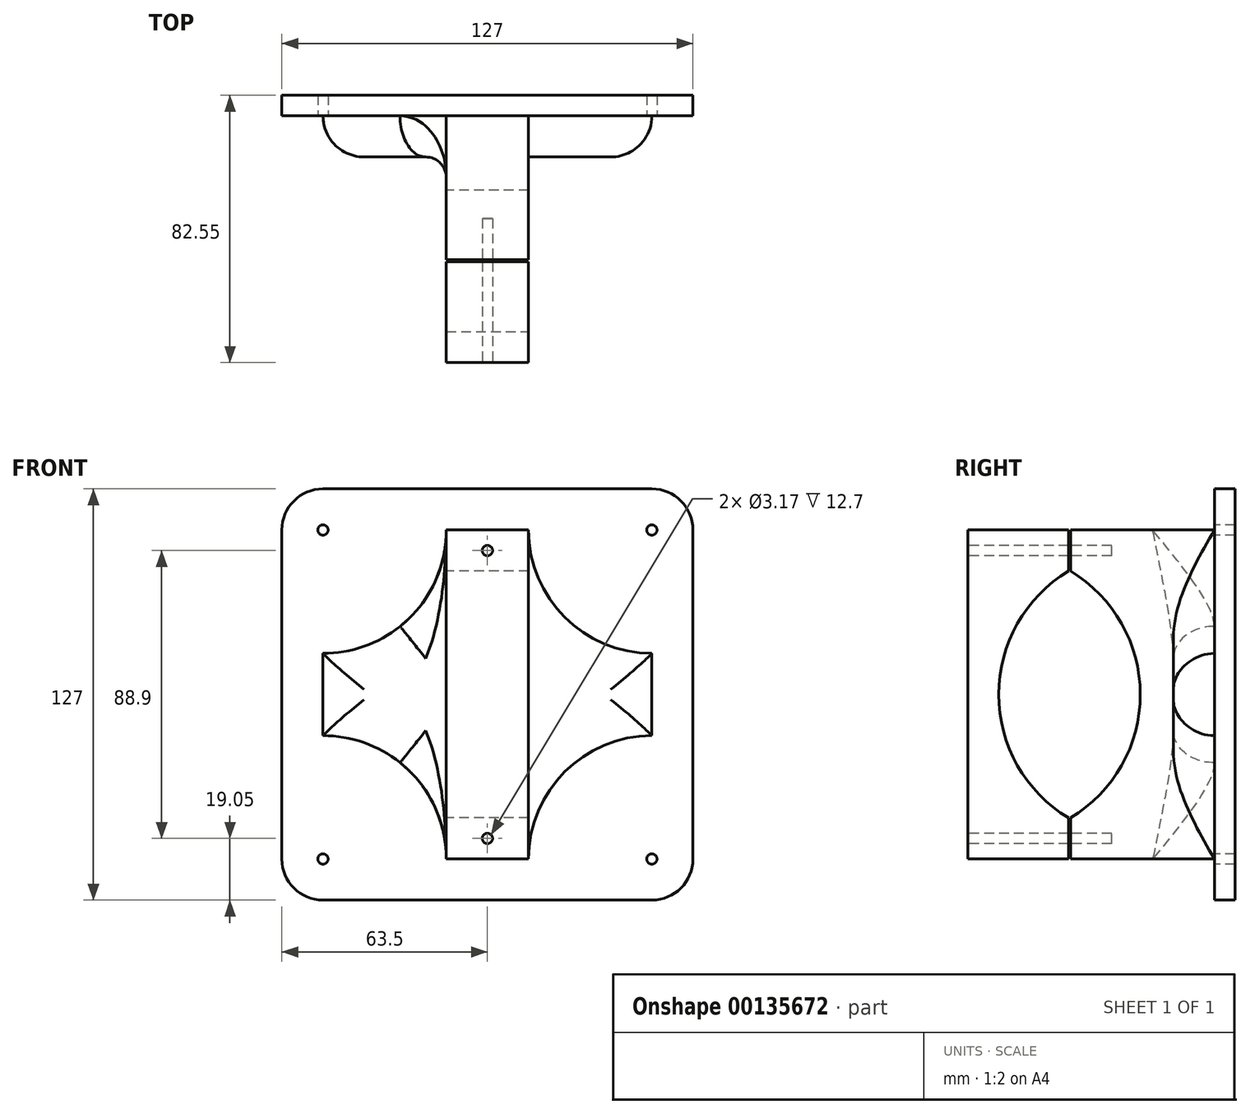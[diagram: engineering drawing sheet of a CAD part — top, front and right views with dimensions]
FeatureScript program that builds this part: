
annotation { "Feature Type Name" : "Feature", "Feature Type Description" : "" }
export const myFeature = defineFeature(function(context is Context, id is Id, definition is map)
    precondition{}
    {
        {
            var Q0;
            Q0=qCreatedBy(makeId("Front.planeOp"),FACE);
            var sketch = newSketch(context, id + "F0", { "sketchPlane" : qUnion([Q0])});
            skLineSegment(sketch, "E0.bottom", {"start": v(63.5, 63.5) * mm, "end": v(-63.5, 63.5) * mm});
            skLineSegment(sketch, "E0.top", {"start": v(63.5, -63.5) * mm, "end": v(-63.5, -63.5) * mm});
            skLineSegment(sketch, "E0.left", {"start": v(63.5, 63.5) * mm, "end": v(63.5, -63.5) * mm});
            skLineSegment(sketch, "E0.right", {"start": v(-63.5, 63.5) * mm, "end": v(-63.5, -63.5) * mm});
            skPoint(sketch, "E0.middle", {"position": v(0, 0) * mm});
            skSolve(sketch);
        }
        {
            var Q0;
            Q0 = qSketchRegion(id + "F0", true);
            extrude(context, id + "F1", {"entities" : qUnion([Q0]), "depth" : 6.35 * mm});
        }
        {
            var Q0;
            Q0=makeQuery(id+"F1.opExtrude","SWEPT_EDGE",EDGE,{"disambiguationData":[OSD([sQuery(id+"F0.wireOp",EDGE,"E0.bottom"),sQuery(id+"F0.wireOp",EDGE,"E0.right")])]});
            var Q1;
            Q1=makeQuery(id+"F1.opExtrude","SWEPT_EDGE",EDGE,{"disambiguationData":[OSD([sQuery(id+"F0.wireOp",EDGE,"E0.bottom"),sQuery(id+"F0.wireOp",EDGE,"E0.left")])]});
            var Q2;
            Q2=makeQuery(id+"F1.opExtrude","SWEPT_EDGE",EDGE,{"disambiguationData":[OSD([sQuery(id+"F0.wireOp",EDGE,"E0.top"),sQuery(id+"F0.wireOp",EDGE,"E0.left")])]});
            var Q3;
            Q3=makeQuery(id+"F1.opExtrude","SWEPT_EDGE",EDGE,{"disambiguationData":[OSD([sQuery(id+"F0.wireOp",EDGE,"E0.top"),sQuery(id+"F0.wireOp",EDGE,"E0.right")])]});
            fillet(context, id + "F2", {"entities" : qUnion([Q0, Q1, Q2, Q3]), "radius" : 12.7 * mm, "tangentPropagation" : true, "allowEdgeOverflow" : false});
        }
        {
            var Q0;
            Q0=makeQuery(id+"F1.opExtrude","CAP_FACE",FACE,{"disambiguationData":[OSD([sQuery(id+"F0.wireOp",EDGE,"E0.bottom"),sQuery(id+"F0.wireOp",EDGE,"E0.top"),sQuery(id+"F0.wireOp",EDGE,"E0.left"),sQuery(id+"F0.wireOp",EDGE,"E0.right")])],"isStart":false});
            var sketch = newSketch(context, id + "F3", { "sketchPlane" : qUnion([Q0])});
            skPoint(sketch, "E1", {"position": v(-50.8, 50.8) * mm});
            skPoint(sketch, "E2", {"position": v(50.8, 50.8) * mm});
            skPoint(sketch, "E3", {"position": v(50.8, -50.8) * mm});
            skPoint(sketch, "E4", {"position": v(-50.8, -50.8) * mm});
            skSolve(sketch);
        }
        {
            var Q0;
            Q0=sQuery(id+"F3.wireOp",VERTEX,"E2");
            var Q1;
            Q1=sQuery(id+"F3.wireOp",VERTEX,"E3");
            var Q2;
            Q2=sQuery(id+"F3.wireOp",VERTEX,"E4");
            var Q3;
            Q3=sQuery(id+"F3.wireOp",VERTEX,"E1");
            var Q4;
            Q4=makeQuery(id+"F1.opExtrude","SWEPT_BODY",BODY,{"disambiguationData":[OSD([sQuery(id+"F0.wireOp",EDGE,"E0.bottom"),sQuery(id+"F0.wireOp",EDGE,"E0.top"),sQuery(id+"F0.wireOp",EDGE,"E0.left"),sQuery(id+"F0.wireOp",EDGE,"E0.right")])]});
            hole(context, id + "F4", {"style" : HoleStyle.SIMPLE, "endStyle" : HoleEndStyle.THROUGH, "holeDiameter" : 3.17 * mm, "locations" : qUnion([Q0, Q1, Q2, Q3]), "scope" : qUnion([Q4]), "isTappedThrough" : true});
        }
        {
            var Q0;
            Q0=makeQuery(id+"F1.opExtrude","CAP_FACE",FACE,{"disambiguationData":[OSD([sQuery(id+"F0.wireOp",EDGE,"E0.bottom"),sQuery(id+"F0.wireOp",EDGE,"E0.top"),sQuery(id+"F0.wireOp",EDGE,"E0.left"),sQuery(id+"F0.wireOp",EDGE,"E0.right")])],"isStart":false});
            var sketch = newSketch(context, id + "F5", { "sketchPlane" : qUnion([Q0])});
            skLineSegment(sketch, "E5.bottom", {"start": v(50.8, 12.7) * mm, "end": v(-50.8, 12.7) * mm});
            skLineSegment(sketch, "E5.top", {"start": v(50.8, -12.7) * mm, "end": v(-50.8, -12.7) * mm});
            skLineSegment(sketch, "E5.left", {"start": v(50.8, 12.7) * mm, "end": v(50.8, -12.7) * mm});
            skLineSegment(sketch, "E5.right", {"start": v(-50.8, 12.7) * mm, "end": v(-50.8, -12.7) * mm});
            skPoint(sketch, "E5.middle", {"position": v(0, 0) * mm});
            skLineSegment(sketch, "E6.bottom", {"start": v(-12.7, 50.8) * mm, "end": v(12.7, 50.8) * mm});
            skLineSegment(sketch, "E6.top", {"start": v(-12.7, -50.8) * mm, "end": v(12.7, -50.8) * mm});
            skLineSegment(sketch, "E6.left", {"start": v(-12.7, 50.8) * mm, "end": v(-12.7, -50.8) * mm});
            skLineSegment(sketch, "E6.right", {"start": v(12.7, 50.8) * mm, "end": v(12.7, -50.8) * mm});
            skArc(sketch, "E7", {"start": v(-50.8, 12.7) * mm, "mid": v(-23.86, 23.86) * mm, "end": v(-12.7, 50.8) * mm});
            skArc(sketch, "E8", {"start": v(12.7, 50.8) * mm, "mid": v(23.86, 23.86) * mm, "end": v(50.8, 12.7) * mm});
            skArc(sketch, "E9", {"start": v(50.8, -12.7) * mm, "mid": v(23.86, -23.86) * mm, "end": v(12.7, -50.8) * mm});
            skArc(sketch, "E10", {"start": v(-12.7, -50.8) * mm, "mid": v(-23.86, -23.86) * mm, "end": v(-50.8, -12.7) * mm});
            skSolve(sketch);
        }
        {
            var Q0;
            {var subQ0=sQuery(id+"F5.wireOp",EDGE,"E8");Q0=makeQuery(id+"F5.imprint","IMPRINT",FACE,{"disambiguationData":[TD([[makeQuery(id+"F5.imprint","IMPRINT",EDGE,{"derivedFrom":subQ0}),-1.0]])]});}
            var Q1;
            {var subQ0=sQuery(id+"F5.wireOp",EDGE,"E7");Q1=makeQuery(id+"F5.imprint","IMPRINT",FACE,{"disambiguationData":[TD([[makeQuery(id+"F5.imprint","IMPRINT",EDGE,{"derivedFrom":subQ0}),-1.0]])]});}
            var Q2;
            {var subQ0=sQuery(id+"F5.wireOp",EDGE,"E9");Q2=makeQuery(id+"F5.imprint","IMPRINT",FACE,{"disambiguationData":[TD([[makeQuery(id+"F5.imprint","IMPRINT",EDGE,{"derivedFrom":subQ0}),-1.0]])]});}
            var Q3;
            {var subQ0=sQuery(id+"F5.wireOp",EDGE,"E10");Q3=makeQuery(id+"F5.imprint","IMPRINT",FACE,{"disambiguationData":[TD([[makeQuery(id+"F5.imprint","IMPRINT",EDGE,{"derivedFrom":subQ0}),-1.0]])]});}
            var Q4;
            {var subQ0=sQuery(id+"F5.wireOp",EDGE,"E5.left");Q4=makeQuery(id+"F5.imprint","IMPRINT",FACE,{"disambiguationData":[TD([[makeQuery(id+"F5.imprint","IMPRINT",EDGE,{"derivedFrom":subQ0}),-1.0]])]});}
            var Q5;
            {var subQ5=sQuery(id+"F5.wireOp",EDGE,"E6.bottom");Q5=makeQuery(id+"F5.imprint","IMPRINT",FACE,{"disambiguationData":[TD([[makeQuery(id+"F5.imprint","IMPRINT",EDGE,{"derivedFrom":subQ5}),-1.0]])]});}
            var Q6;
            {var subQ5=sQuery(id+"F5.wireOp",EDGE,"E6.top");Q6=makeQuery(id+"F5.imprint","IMPRINT",FACE,{"disambiguationData":[TD([[makeQuery(id+"F5.imprint","IMPRINT",EDGE,{"derivedFrom":subQ5}),1.0]])]});}
            var Q7;
            {var subQ0=sQuery(id+"F5.wireOp",EDGE,"E6.right");var subQ1=sQuery(id+"F5.wireOp",EDGE,"E5.bottom");var subQ2=makeQuery(id+"F5.imprint","INTERSECT",VERTEX,{"derivedFrom":[subQ1,subQ0]});Q7=makeQuery(id+"F5.imprint","IMPRINT",FACE,{"disambiguationData":[TD([[makeQuery(id+"F5.imprint","IMPRINT",EDGE,{"disambiguationData":[TD([[subQ2,-1.0]])],"derivedFrom":subQ1}),1.0]])]});}
            var Q8;
            {var subQ0=sQuery(id+"F5.wireOp",EDGE,"E5.right");Q8=makeQuery(id+"F5.imprint","IMPRINT",FACE,{"disambiguationData":[TD([[makeQuery(id+"F5.imprint","IMPRINT",EDGE,{"derivedFrom":subQ0}),1.0]])]});}
            extrude(context, id + "F6", {"entities" : qUnion([Q0, Q1, Q2, Q3, Q4, Q5, Q6, Q7, Q8]), "operationType" : NewBodyOperationType.ADD, "depth" : 12.7 * mm});
        }
        {
            var Q0;
            Q0=qCreatedBy(makeId("Right.planeOp"),FACE);
            var sketch = newSketch(context, id + "F7", { "sketchPlane" : qUnion([Q0])});
            skLineSegment(sketch, "E11", {"start": v(-50.8, -50.8) * mm, "end": v(-19.05, -50.8) * mm});
            skLineSegment(sketch, "E12", {"start": v(-19.05, -50.8) * mm, "end": v(-19.05, 50.8) * mm});
            skLineSegment(sketch, "E13", {"start": v(-19.05, 50.8) * mm, "end": v(-50.8, 50.8) * mm});
            skLineSegment(sketch, "E14", {"start": v(-50.8, -50.8) * mm, "end": v(-50.8, -38.1) * mm});
            skLineSegment(sketch, "E15", {"start": v(-50.8, 50.8) * mm, "end": v(-50.8, 38.1) * mm});
            skArc(sketch, "E16", {"start": v(-50.8, -38.1) * mm, "mid": v(-29.25, 0) * mm, "end": v(-50.8, 38.1) * mm});
            skSolve(sketch);
        }
        {
            var Q0;
            Q0 = qSketchRegion(id + "F7", true);
            extrude(context, id + "F8", {"entities" : qUnion([Q0]), "operationType" : NewBodyOperationType.ADD, "endBound" : BoundingType.SYMMETRIC, "depth" : 25.4 * mm});
        }
        {
            var Q0;
            Q0=makeQuery(id+"F8.opExtrude","CAP_EDGE",EDGE,{"disambiguationData":[OSD([sQuery(id+"F7.wireOp",EDGE,"E12")])],"isStart":false});
            var Q1;
            Q1=makeQuery(id+"F8.opExtrude","CAP_EDGE",EDGE,{"disambiguationData":[OSD([sQuery(id+"F7.wireOp",EDGE,"E12")])],"isStart":true});
            fillet(context, id + "F9", {"entities" : qUnion([Q0, Q1]), "radius" : 6.35 * mm, "tangentPropagation" : true, "allowEdgeOverflow" : false});
        }
        {
            var Q0;
            Q0=makeQuery(id+"F9.opFillet","BLEND_EDGE",EDGE,{"blendedFrom":[makeQuery(id+"F8.opExtrude","CAP_EDGE",EDGE,{"disambiguationData":[OSD([sQuery(id+"F7.wireOp",EDGE,"E12")])],"isStart":false}),makeQuery(id+"F6.opExtrude","SWEPT_FACE",FACE,{"disambiguationData":[OSD([sQuery(id+"F5.wireOp",EDGE,"E9")])]})],"blendedInto":[makeQuery(id+"F6.opExtrude","SWEPT_FACE",FACE,{"disambiguationData":[OSD([sQuery(id+"F5.wireOp",EDGE,"E9")])]})]});
            var Q1;
            Q1=makeQuery(id+"F6.opExtrude","CAP_EDGE",EDGE,{"disambiguationData":[OSD([sQuery(id+"F5.wireOp",EDGE,"E9")])],"isStart":false});
            var Q2;
            Q2=makeQuery(id+"F6.opExtrude","CAP_EDGE",EDGE,{"disambiguationData":[OSD([sQuery(id+"F5.wireOp",EDGE,"E5.left")])],"isStart":false});
            var Q3;
            Q3=makeQuery(id+"F6.opExtrude","CAP_EDGE",EDGE,{"disambiguationData":[OSD([sQuery(id+"F5.wireOp",EDGE,"E8")])],"isStart":false});
            var Q4;
            Q4=makeQuery(id+"F9.opFillet","BLEND_EDGE",EDGE,{"blendedFrom":[makeQuery(id+"F8.opExtrude","CAP_EDGE",EDGE,{"disambiguationData":[OSD([sQuery(id+"F7.wireOp",EDGE,"E12")])],"isStart":false}),makeQuery(id+"F6.opExtrude","SWEPT_FACE",FACE,{"disambiguationData":[OSD([sQuery(id+"F5.wireOp",EDGE,"E8")])]})],"blendedInto":[makeQuery(id+"F6.opExtrude","SWEPT_FACE",FACE,{"disambiguationData":[OSD([sQuery(id+"F5.wireOp",EDGE,"E8")])]})]});
            var Q5;
            Q5=makeQuery(id+"F9.opFillet","BLEND_EDGE",EDGE,{"blendedFrom":[makeQuery(id+"F8.opExtrude","CAP_EDGE",EDGE,{"disambiguationData":[OSD([sQuery(id+"F7.wireOp",EDGE,"E12")])],"isStart":true}),makeQuery(id+"F6.opExtrude","SWEPT_FACE",FACE,{"disambiguationData":[OSD([sQuery(id+"F5.wireOp",EDGE,"E10")])]})],"blendedInto":[makeQuery(id+"F6.opExtrude","SWEPT_FACE",FACE,{"disambiguationData":[OSD([sQuery(id+"F5.wireOp",EDGE,"E10")])]})]});
            var Q6;
            Q6=makeQuery(id+"F6.opExtrude","CAP_EDGE",EDGE,{"disambiguationData":[OSD([sQuery(id+"F5.wireOp",EDGE,"E10")])],"isStart":false});
            var Q7;
            Q7=makeQuery(id+"F6.opExtrude","CAP_EDGE",EDGE,{"disambiguationData":[OSD([sQuery(id+"F5.wireOp",EDGE,"E5.right")])],"isStart":false});
            var Q8;
            Q8=makeQuery(id+"F6.opExtrude","CAP_EDGE",EDGE,{"disambiguationData":[OSD([sQuery(id+"F5.wireOp",EDGE,"E7")])],"isStart":false});
            var Q9;
            Q9=makeQuery(id+"F9.opFillet","BLEND_EDGE",EDGE,{"blendedFrom":[makeQuery(id+"F8.opExtrude","CAP_EDGE",EDGE,{"disambiguationData":[OSD([sQuery(id+"F7.wireOp",EDGE,"E12")])],"isStart":true}),makeQuery(id+"F6.opExtrude","SWEPT_FACE",FACE,{"disambiguationData":[OSD([sQuery(id+"F5.wireOp",EDGE,"E7")])]})],"blendedInto":[makeQuery(id+"F6.opExtrude","SWEPT_FACE",FACE,{"disambiguationData":[OSD([sQuery(id+"F5.wireOp",EDGE,"E7")])]})]});
            fillet(context, id + "F10", {"entities" : qUnion([Q0, Q1, Q2, Q3, Q4, Q5, Q6, Q7, Q8, Q9]), "radius" : 12.7 * mm, "tangentPropagation" : true, "allowEdgeOverflow" : false});
        }
        {
            var Q0;
            Q0=makeQuery(id+"F8.opExtrude","SWEPT_FACE",FACE,{"disambiguationData":[OSD([sQuery(id+"F7.wireOp",EDGE,"E14")])]});
            cPlane(context, id + "F11", {"entities" : qUnion([Q0]), "cplaneType" : CPlaneType.OFFSET, "offset" : 31.75 * mm, "width" : 152.4 * mm, "height" : 152.4 * mm});
        }
        {
            var Q0;
            Q0=qCreatedBy(id+"F11.planeOp",FACE);
            var sketch = newSketch(context, id + "F12", { "sketchPlane" : qUnion([Q0])});
            skLineSegment(sketch, "E17.bottom", {"start": v(-12.7, 50.8) * mm, "end": v(12.7, 50.8) * mm});
            skLineSegment(sketch, "E17.top", {"start": v(-12.7, -50.8) * mm, "end": v(12.7, -50.8) * mm});
            skLineSegment(sketch, "E17.left", {"start": v(-12.7, 50.8) * mm, "end": v(-12.7, -50.8) * mm});
            skLineSegment(sketch, "E17.right", {"start": v(12.7, 50.8) * mm, "end": v(12.7, -50.8) * mm});
            skSolve(sketch);
        }
        {
            var Q0;
            Q0 = qSketchRegion(id + "F12", true);
            extrude(context, id + "F13", {"entities" : qUnion([Q0]), "oppositeDirection" : true, "depth" : 31.12 * mm});
        }
        {
            var Q0;
            Q0=makeQuery(id+"F13.opExtrude","SWEPT_FACE",FACE,{"disambiguationData":[OSD([sQuery(id+"F12.wireOp",EDGE,"E17.right")])]});
            var sketch = newSketch(context, id + "F14", { "sketchPlane" : qUnion([Q0])});
            skLineSegment(sketch, "E18", {"start": v(-51.44, 50.8) * mm, "end": v(-51.44, 38.1) * mm});
            skLineSegment(sketch, "E19", {"start": v(-51.44, -50.8) * mm, "end": v(-51.44, -38.1) * mm});
            skArc(sketch, "E20", {"start": v(-51.44, 38.1) * mm, "mid": v(-72.99, 0) * mm, "end": v(-51.43, -38.1) * mm});
            skLineSegment(sketch, "E21", {"start": v(-51.44, 38.1) * mm, "end": v(-51.44, -38.1) * mm});
            skSolve(sketch);
        }
        {
            var Q0;
            Q0 = qSketchRegion(id + "F14", true);
            extrude(context, id + "F15", {"entities" : qUnion([Q0]), "operationType" : NewBodyOperationType.REMOVE, "endBound" : BoundingType.THROUGH_ALL, "oppositeDirection" : true, "depth" : 25.4 * mm});
        }
        {
            var Q0;
            Q0=makeQuery(id+"F13.opExtrude","CAP_FACE",FACE,{"disambiguationData":[OSD([sQuery(id+"F12.wireOp",EDGE,"E17.bottom"),sQuery(id+"F12.wireOp",EDGE,"E17.top"),sQuery(id+"F12.wireOp",EDGE,"E17.left"),sQuery(id+"F12.wireOp",EDGE,"E17.right")])],"isStart":true});
            var sketch = newSketch(context, id + "F16", { "sketchPlane" : qUnion([Q0])});
            skLineSegment(sketch, "E22", {"start": v(0, 50.8) * mm, "end": v(0, 44.45) * mm, "construction": true});
            skPoint(sketch, "E22.endSnap0", {"position": v(0, 50.8) * mm});
            skLineSegment(sketch, "E23", {"start": v(0, -50.8) * mm, "end": v(0, -44.45) * mm, "construction": true});
            skPoint(sketch, "E23.endSnap0", {"position": v(0, -50.8) * mm});
            skCircle(sketch, "E24", {"center": v(0, 44.45) * mm, "radius": 1.59 * mm});
            skCircle(sketch, "E25", {"center": v(0, -44.45) * mm, "radius": 1.59 * mm});
            skSolve(sketch);
        }
        {
            var Q0;
            Q0 = qSketchRegion(id + "F16", true);
            extrude(context, id + "F17", {"entities" : qUnion([Q0]), "operationType" : NewBodyOperationType.REMOVE, "oppositeDirection" : true, "depth" : 44.45 * mm});
        }
        {
            var Q0;
            Q0=makeQuery(id+"F8.opExtrude","SWEPT_FACE",FACE,{"disambiguationData":[OSD([sQuery(id+"F7.wireOp",EDGE,"E15")])]});
            var sketch = newSketch(context, id + "F18", { "sketchPlane" : qUnion([Q0])});
            skLineSegment(sketch, "E26", {"start": v(0, 50.8) * mm, "end": v(0, 44.45) * mm, "construction": true});
            skPoint(sketch, "E26.endSnap0", {"position": v(0, 50.8) * mm});
            skLineSegment(sketch, "E27", {"start": v(0, -44.45) * mm, "end": v(0, -50.8) * mm, "construction": true});
            skCircle(sketch, "E28", {"center": v(0, 44.45) * mm, "radius": 1.59 * mm});
            skCircle(sketch, "E29", {"center": v(0, -44.45) * mm, "radius": 1.59 * mm});
            skSolve(sketch);
        }
        {
            var Q0;
            Q0 = qSketchRegion(id + "F18", true);
            extrude(context, id + "F19", {"entities" : qUnion([Q0]), "operationType" : NewBodyOperationType.REMOVE, "oppositeDirection" : true, "depth" : 12.7 * mm});
        }
    });
